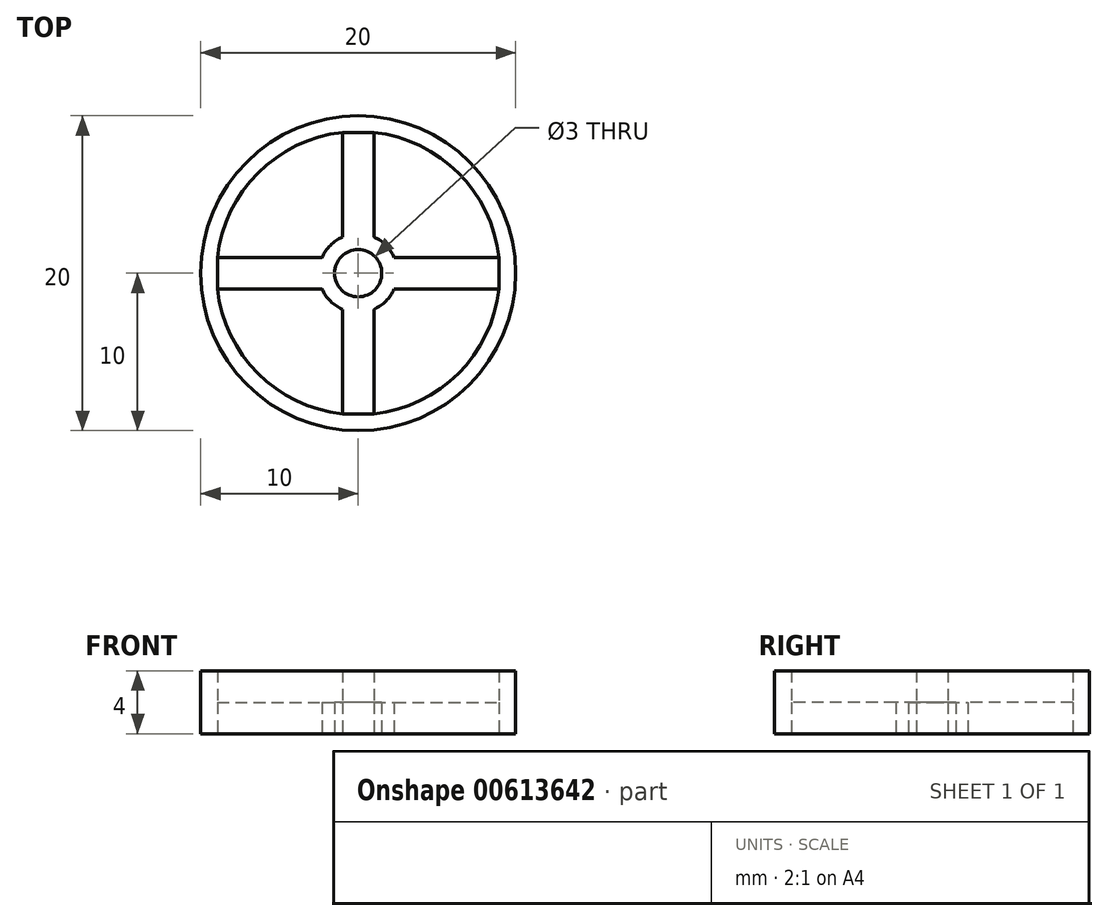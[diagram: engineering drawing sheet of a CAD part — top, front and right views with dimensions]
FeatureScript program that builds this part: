
annotation { "Feature Type Name" : "Feature", "Feature Type Description" : "" }
export const myFeature = defineFeature(function(context is Context, id is Id, definition is map)
    precondition{}
    {
        {
            var Q0;
            Q0=qCreatedBy(makeId("Top.planeOp"),FACE);
            var sketch = newSketch(context, id + "F0", { "sketchPlane" : qUnion([Q0])});
            skCircle(sketch, "E0", {"center": v(0, 0) * mm, "radius": 10 * mm});
            skArc(sketch, "E1", {"start": v(-8.94, -1) * mm, "mid": v(-6.36, -6.36) * mm, "end": v(-1, -8.94) * mm});
            skArc(sketch, "E2", {"start": v(-1, 2.3) * mm, "mid": v(-1.77, 1.77) * mm, "end": v(-2.3, 1) * mm});
            skLineSegment(sketch, "E3", {"start": v(-8.94, 1) * mm, "end": v(-2.3, 1) * mm});
            skLineSegment(sketch, "E4", {"start": v(-8.94, -1) * mm, "end": v(-2.3, -1) * mm});
            skLineSegment(sketch, "E5", {"start": v(-1, 8.94) * mm, "end": v(-1, 2.3) * mm});
            skLineSegment(sketch, "E6", {"start": v(1, 8.94) * mm, "end": v(1, 2.3) * mm});
            skPoint(sketch, "E7.start.orphan", {"position": v(0, 9) * mm});
            skLineSegment(sketch, "E8.trimOffspring", {"start": v(2.3, -1) * mm, "end": v(8.94, -1) * mm});
            skLineSegment(sketch, "E9.trimOffspring", {"start": v(2.3, 1) * mm, "end": v(8.94, 1) * mm});
            skLineSegment(sketch, "E10.trimOffspring", {"start": v(1, -2.3) * mm, "end": v(1, -8.94) * mm});
            skLineSegment(sketch, "E11.trimOffspring", {"start": v(-1, -2.3) * mm, "end": v(-1, -8.94) * mm});
            skPoint(sketch, "E12.orphan", {"position": v(-1, -9.95) * mm});
            skPoint(sketch, "E13.orphan", {"position": v(1, -9.95) * mm});
            skArc(sketch, "E14.trimOffspring", {"start": v(1, -2.3) * mm, "mid": v(1.77, -1.77) * mm, "end": v(2.3, -1) * mm});
            skPoint(sketch, "E15.start.orphan", {"position": v(2.5, 0) * mm});
            skArc(sketch, "E16.trimOffspring", {"start": v(2.3, 1) * mm, "mid": v(1.77, 1.77) * mm, "end": v(1, 2.3) * mm});
            skPoint(sketch, "E17.start.orphan", {"position": v(-2.5, 0) * mm});
            skArc(sketch, "E18.trimOffspring", {"start": v(-2.3, -1) * mm, "mid": v(-1.77, -1.77) * mm, "end": v(-1, -2.3) * mm});
            skArc(sketch, "E19.trimOffspring", {"start": v(-1, 8.94) * mm, "mid": v(-6.36, 6.36) * mm, "end": v(-8.94, 1) * mm});
            skArc(sketch, "E20.trimOffspring", {"start": v(8.94, 1) * mm, "mid": v(6.36, 6.36) * mm, "end": v(1, 8.94) * mm});
            skArc(sketch, "E21.trimOffspring", {"start": v(1, -8.94) * mm, "mid": v(6.36, -6.36) * mm, "end": v(8.94, -1) * mm});
            skLineSegment(sketch, "E22", {"start": v(-8.94, 1) * mm, "end": v(-8.94, -1) * mm});
            skLineSegment(sketch, "E23", {"start": v(-1, 8.94) * mm, "end": v(1, 8.94) * mm});
            skLineSegment(sketch, "E24", {"start": v(8.94, 1) * mm, "end": v(8.94, -1) * mm});
            skLineSegment(sketch, "E25", {"start": v(1, -8.94) * mm, "end": v(-1, -8.94) * mm});
            skCircle(sketch, "E26", {"center": v(0, 0) * mm, "radius": 1.5 * mm});
            skSolve(sketch);
        }
        {
            var Q0;
            Q0=makeQuery(id+"F0.imprint","IMPRINT",FACE,{"disambiguationData":[TD([[makeQuery(id+"F0.imprint","IMPRINT",EDGE,{"derivedFrom":sQuery(id+"F0.wireOp",EDGE,"E2")}),1.0]])]});
            extrude(context, id + "F1", {"entities" : qUnion([Q0]), "depth" : 2 * mm, "offsetDistance" : 25 * mm});
        }
        {
            var Q0;
            Q0=makeQuery(id+"F0.imprint","IMPRINT",FACE,{"disambiguationData":[TD([[makeQuery(id+"F0.imprint","IMPRINT",EDGE,{"derivedFrom":sQuery(id+"F0.wireOp",EDGE,"E0")}),1.0]])]});
            extrude(context, id + "F2", {"entities" : qUnion([Q0]), "operationType" : NewBodyOperationType.ADD, "depth" : 4 * mm, "offsetDistance" : 25 * mm});
        }
    });
